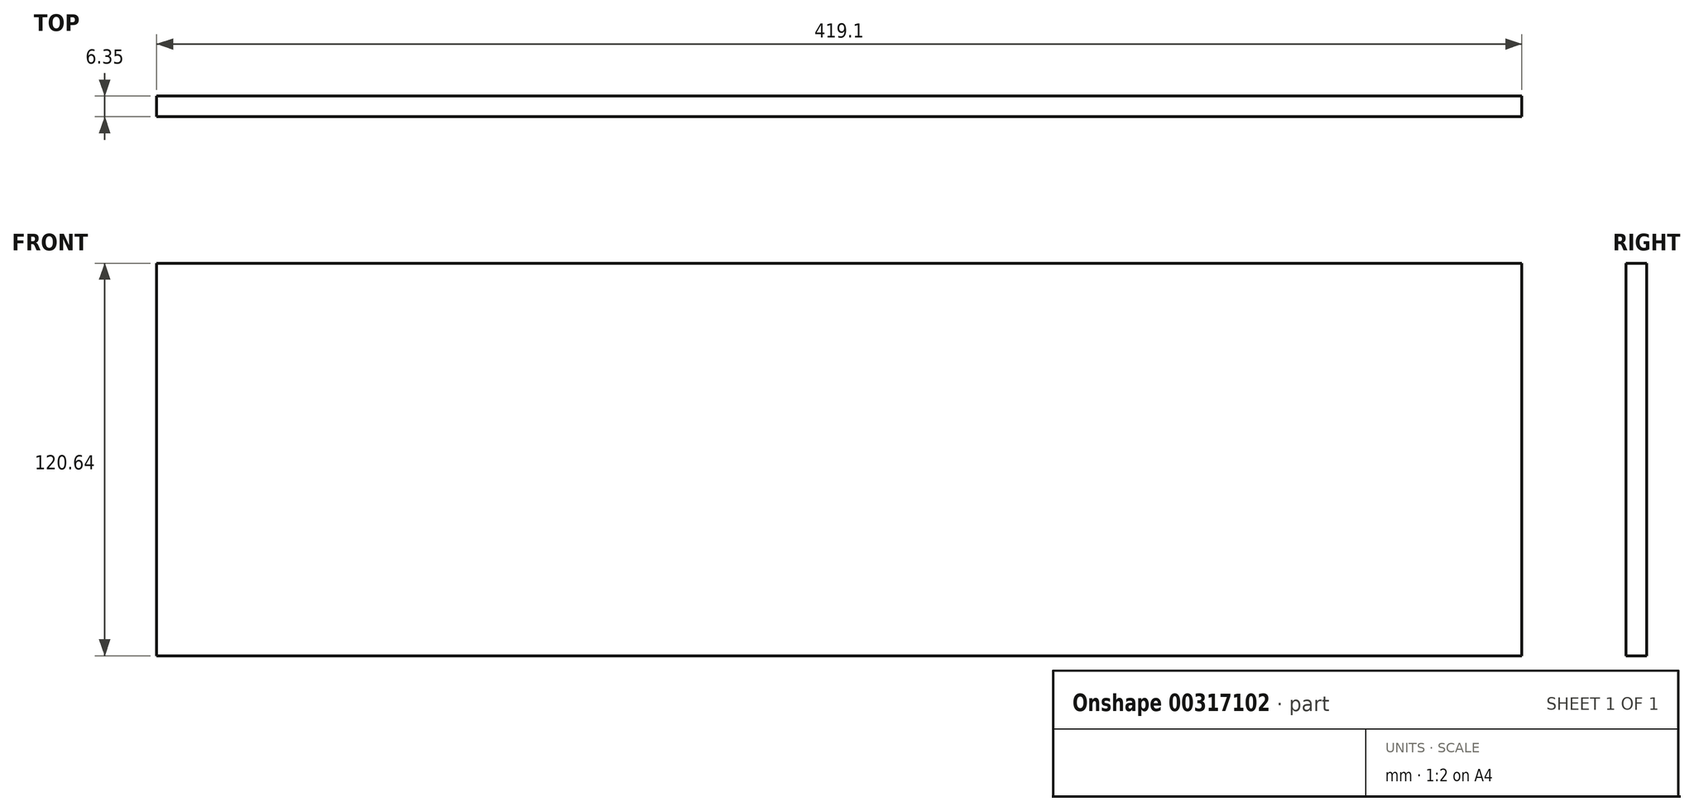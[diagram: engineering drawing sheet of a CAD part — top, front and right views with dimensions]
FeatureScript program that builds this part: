
annotation { "Feature Type Name" : "Feature", "Feature Type Description" : "" }
export const myFeature = defineFeature(function(context is Context, id is Id, definition is map)
    precondition{}
    {
        {
            var Q0;
            Q0=qCreatedBy(makeId("Front.planeOp"),FACE);
            var sketch = newSketch(context, id + "F0", { "sketchPlane" : qUnion([Q0])});
            skLineSegment(sketch, "E0.bottom", {"start": v(209.55, 60.33) * mm, "end": v(-209.55, 60.32) * mm});
            skLineSegment(sketch, "E0.top", {"start": v(209.55, -60.32) * mm, "end": v(-209.55, -60.33) * mm});
            skLineSegment(sketch, "E0.left", {"start": v(209.55, 60.33) * mm, "end": v(209.55, -60.32) * mm});
            skLineSegment(sketch, "E0.right", {"start": v(-209.55, 60.32) * mm, "end": v(-209.55, -60.33) * mm});
            skPoint(sketch, "E0.middle", {"position": v(0, 0) * mm});
            skSolve(sketch);
        }
        {
            var Q0;
            Q0 = qSketchRegion(id + "F0", true);
            extrude(context, id + "F1", {"entities" : qUnion([Q0]), "depth" : 6.35 * mm});
        }
    });
